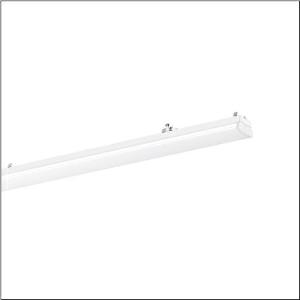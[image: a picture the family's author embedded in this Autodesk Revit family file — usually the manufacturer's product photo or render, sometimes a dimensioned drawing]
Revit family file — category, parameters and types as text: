
# Revit family: licross_r__11_recessed_opal_ho_51tl1ddn4d5m_587a
name_source: partatom
category: Lighting Fixtures
units: mm (PartAtom-declared; Revit-internal decimal feet)

## family parameters
Cut with Voids When Loaded = No
Host = Face
Light Source = No
Part Type = Normal
Room Calculation Point = No
Round Connector Dimension = Use Diameter
Shared = No

## types (1)
- --- (1 x LED, 13620 lm, 76.8 W, 4000K)
    Apparent Load = 77 VA
    CIE Flux Codes = 44 73 91 87 100
    Color Rendering = 80
    Color Temperature = 4000K
    Default Elevation = 1800 mm
    Description = Licross® 11 recessed opal HO, luminaire insert, of sheet steel, coil coated, white, length: 1.500mm, width: 76mm, height: 87mm, LED rated luminous flux: 13.620lm, light colour: 840, control gear: DALI 2, with plug, 5-pole, with phase selection, mains connection: 220..240V, AC, 50/60Hz, rated input power: 77W, halogen-free wiring, primary optical cover: cover, of PMMA, light emission: direct with ceiling illumination distribution, primary light characteristic: symmetric, protection rating (complete): IP40, insulation class (complete): insulation class I (protective earthing), certification: CE, ENEC, VDE, UKCA, protection symbol: D if used in an environment without relevant dust loads with corresponding accessories, impact resistance: IK06, permissible ambient temperature for indoor applications: -25..+30°C, corresponds to IFS (International Featured Standards) requirements for safety and quality in the food industry, reducing of maximum allowable ambient temperature of 5°C with ceiling mounting, LABS conformity tested according to VDMA 24364:2018-05, packaging unit: 1 piece
    Height = 83 mm
    Lamp = 1 x LED
    Lamp Light Flux = 13620 lm
    Lamp Power = 76.8 W
    Lamp count = 1
    Length = 1500 mm
    Luminous efficacy = 177 lm/W
    Manufacturer = Siteco
    ModVariant = No
    Model = 51TL1DDN4D5M
    Mounting Place = Ceiling
    Mounting Type = Pendant
    Number of Poles = 1
    OnlyDefault = Yes
    Power Factor = 1
    Product Name = Licross® 11 recessed opal HO
    Product group = luminaire insert
    ProductGroupID = 901
    Protection Class = Protection class I
    Protection Degree = IP 40
    RLX_Detail_Level = 1
    RLX_Emergency_Light_Flux = 0 lm
    RLX_Emergency_Type = 0
    RLX_Emergency_Type_DB = No
    RlxData = <blob elided: 18209 chars, md5=af544f96>
    Socket = socket
    Standby Power = 0 W
    System Light Flux = 13620 lm
    System Power = 77 W
    Type Comments = factory setting: luminous flux: 100 % | dim-lin: 254 | 522 mA
    Type Image = l_1313666.jpg
    URL = http://relux.com
    VarID = @adj_027307
    Voltage = 0 V
    Weight = 0.00 kg
    Width = 76 mm

## geometry (parser evidence)
native form markers: Blend x4, Sweep x12
no freeform markers — native parametric forms only
